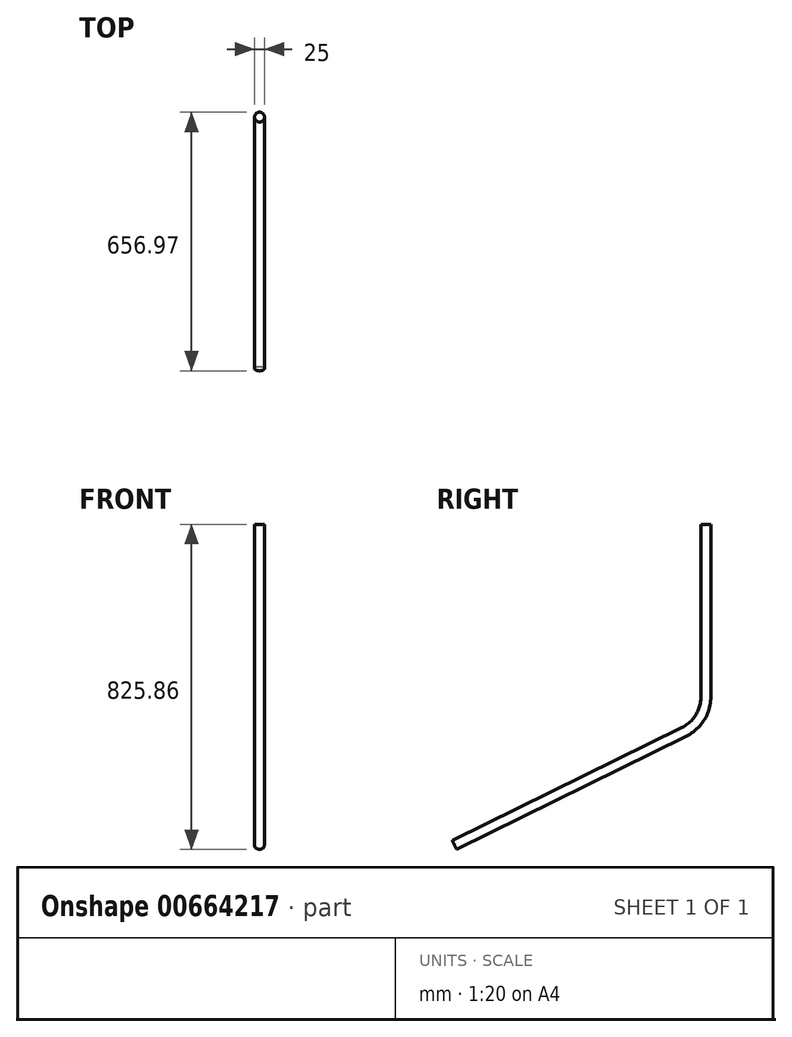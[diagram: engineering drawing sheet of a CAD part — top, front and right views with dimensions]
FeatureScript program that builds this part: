
annotation { "Feature Type Name" : "Feature", "Feature Type Description" : "" }
export const myFeature = defineFeature(function(context is Context, id is Id, definition is map)
    precondition{}
    {
        {
            var Q0;
            Q0=qCreatedBy(makeId("Right.planeOp"),FACE);
            var sketch = newSketch(context, id + "F0", { "sketchPlane" : qUnion([Q0])});
            skLineSegment(sketch, "E0", {"start": v(0, 794.56) * mm, "end": v(0, 356.78) * mm});
            skLineSegment(sketch, "E1", {"start": v(-638.95, -20.09) * mm, "end": v(-55.82, 267.07) * mm});
            skPoint(sketch, "E2.visualSharp", {"position": v(0, 294.56) * mm});
            skArc(sketch, "E2.filletArc", {"start": v(-55.82, 267.07) * mm, "mid": v(-15.1, 303.95) * mm, "end": v(0, 356.78) * mm});
            skSolve(sketch);
        }
        {
            var Q0;
            Q0=sQuery(id+"F0.wireOp",VERTEX,"E0.start");
            var Q1;
            Q1=sQuery(id+"F0.wireOp",EDGE,"E0");
            cPlane(context, id + "F1", {"entities" : qUnion([Q0, Q1]), "cplaneType" : CPlaneType.LINE_POINT, "offset" : 25 * mm, "width" : 150 * mm, "height" : 150 * mm});
        }
        {
            var Q0;
            Q0=qCreatedBy(id+"F1.planeOp",FACE);
            var sketch = newSketch(context, id + "F2", { "sketchPlane" : qUnion([Q0])});
            skCircle(sketch, "E3", {"center": v(0, 0) * mm, "radius": 12.5 * mm});
            skSolve(sketch);
        }
        {
            var Q0;
            Q0=makeQuery(id+"F2.imprint","IMPRINT",FACE,{"disambiguationData":[TD([[makeQuery(id+"F2.imprint","IMPRINT",EDGE,{"derivedFrom":sQuery(id+"F2.wireOp",EDGE,"E3")}),1.0]])]});
            var Q1;
            Q1=sQuery(id+"F0.wireOp",EDGE,"E0");
            var Q2;
            Q2=sQuery(id+"F0.wireOp",EDGE,"E2.filletArc");
            var Q3;
            Q3=sQuery(id+"F0.wireOp",EDGE,"E1");
            sweep(context, id + "F3", {"profiles" : qUnion([Q0]), "path" : qUnion([Q1, Q2, Q3])});
        }
    });
